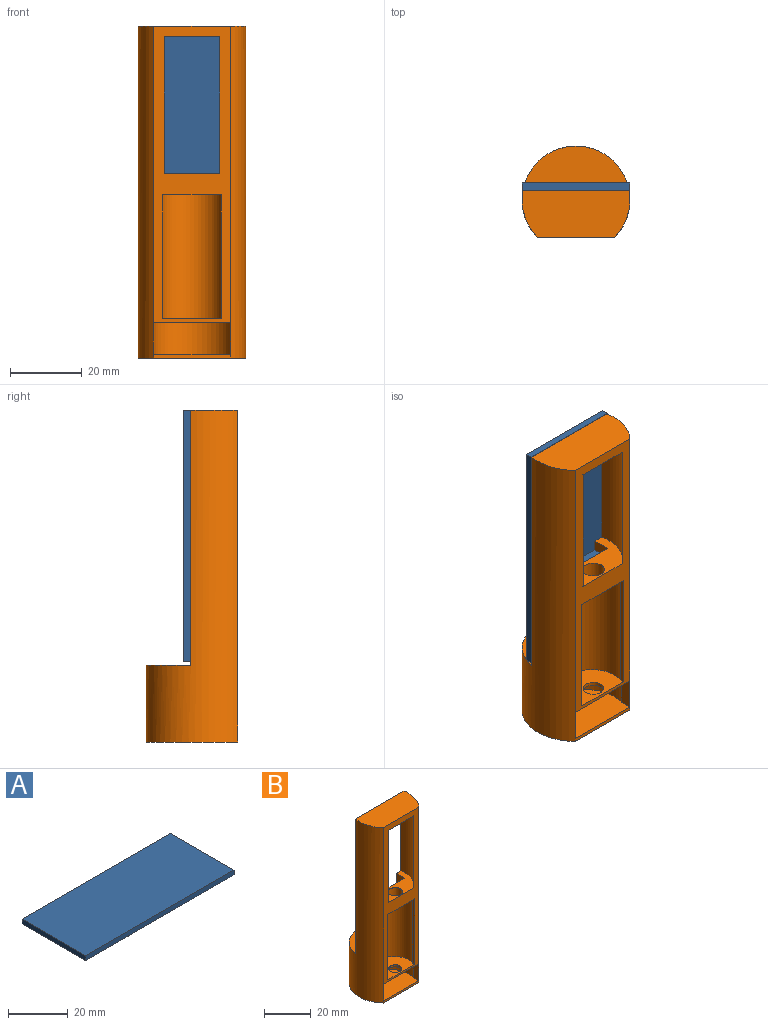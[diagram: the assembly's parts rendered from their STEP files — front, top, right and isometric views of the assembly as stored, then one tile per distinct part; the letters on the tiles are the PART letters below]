
ASSEMBLY  parts=2 mates=1
PART A: 11 faces, bbox 70x30x7 mm
  f0: plane 70x2mm, normal (0,1,0), area 140mm2, adj f1,f3,f4,f5
  f1: plane 30x2mm, normal (-1,0,0), area 60mm2, adj f0,f2,f4,f5
  f2: plane 70x2mm, normal (0,-1,0), area 140mm2, adj f1,f3,f4,f5
  f3: plane 30x2mm, normal (1,0,0), area 60mm2, adj f0,f2,f4,f5
  f4: plane 70x30mm, normal (0,0,1), area 2100mm2, adj f0,f1,f2,f3
  f5: plane 70x30mm, normal (0,0,-1), area 2060mm2, adj f0,f1,f2,f3,f6,f7,f8,f9
  f6: plane 5x2mm, normal (0,-1,0), area 10mm2, adj f5,f7,f9,f10
  f7: plane 20x5mm, normal (-1,0,0), area 100mm2, adj f5,f6,f8,f10
  f8: plane 5x2mm, normal (0,1,0), area 10mm2, adj f5,f7,f9,f10
  f9: plane 20x5mm, normal (1,0,0), area 100mm2, adj f5,f6,f8,f10
  f10: plane 20x2mm, normal (0,0,-1), area 40mm2, adj f6,f7,f8,f9
PART B: 27 faces, bbox 30x25.5x92.4 mm
  f0: plane 26x13.1mm, normal (0,0,1), area 176.3mm2, adj f14,f16,f17,f19,f20,f21,f23,f24
  f1: plane 17.4x12.9mm, normal (0,0,1), area 164.2mm2, adj f9,f10,f11,f12,f17
  f2: plane 8.9x3.39mm, normal (-1,0,0), area 30.2mm2, adj f3,f5,f6,f8
  f3: cylinder r=15mm len=92.4mm, axis (0,0,-1), area 3528mm2, adj f2,f4,f6,f7,f8,f15,f16,f17
  f4: plane 8.9x3.39mm, normal (1,0,0), area 30.2mm2, adj f3,f5,f6,f8
  f5: cylinder r=11.25mm len=22.5mm, axis (0,0,-1), area 374.5mm2, adj f2,f4,f6,f8
  f6: plane 22.5x18mm, normal (0,0,1), area 346.1mm2, adj f2,f3,f4,f5,f18
  f7: plane 30x25.5mm, normal (0,0,-1), area 640.4mm2, adj f3,f18
  f8: plane 22.5x18mm, normal (0,0,-1), area 320.6mm2, adj f2,f3,f4,f5,f9,f17
  f9: cylinder r=2.85mm len=5.7mm, axis (0,0,-1), area 17.9mm2, adj f1,f8
  f10: plane 34.5x1.29mm, normal (-1,0,0), area 44.6mm2, adj f1,f12,f13,f17
  f11: plane 34.5x1.29mm, normal (1,0,0), area 44.6mm2, adj f1,f12,f13,f17
  f12: cylinder r=8.7mm len=34.5mm, axis (0,0,-1), area 1147.5mm2, adj f1,f10,f11,f13
  f13: plane 17.4x12.9mm, normal (0,0,-1), area 159.5mm2, adj f10,f11,f12,f14,f17
  f14: cylinder r=3.1mm len=6.2mm, axis (0,0,-1), area 116.9mm2, adj f0,f13
  f15: plane 29.55x12.4mm, normal (0,0,1), area 275.8mm2, adj f3,f16
  f16: plane 71x29.55mm, normal (0,1,0), area 1029.7mm2, adj f0,f3,f15,f19,f21,f22,f23,f24
  f17: plane 82.5x21.42mm, normal (0,-1,0), area 619.2mm2, adj f0,f1,f3,f8,f10,f11,f13,f23
  f18: plane 21.42x1mm, normal (0,-1,0), area 21.4mm2, adj f3,f6,f7
  f19: plane 5x5mm, normal (1,0,0), area 25mm2, adj f0,f16,f20,f22
  f20: plane 20x5mm, normal (0,1,0), area 100mm2, adj f0,f19,f21,f22
  f21: plane 5x5mm, normal (-1,0,0), area 25mm2, adj f0,f16,f20,f22
  f22: plane 20x5mm, normal (0,0,1), area 100mm2, adj f16,f19,f20,f21
  f23: cylinder r=13mm len=38mm, axis (0,0,-1), area 563.9mm2, adj f0,f16,f17,f25
  f24: cylinder r=13mm len=38mm, axis (0,0,-1), area 563.9mm2, adj f0,f16,f17,f25
  f25: plane 26x13.1mm, normal (0,0,-1), area 306.5mm2, adj f16,f17,f23,f24
  f26: plane 30x13.1mm, normal (0,0,1), area 364.5mm2, adj f3,f16,f17
PLACE A rot(axis=(-0.58,-0.58,-0.58),120deg) t=(-5.56,18.69,41.58)mm
PLACE B t=(-5.56,16.09,-14.82)mm
MATE fastened B.f22 <-> A.f7  axis (0,0,1) through (-5.56,16.19,30.58)mm
